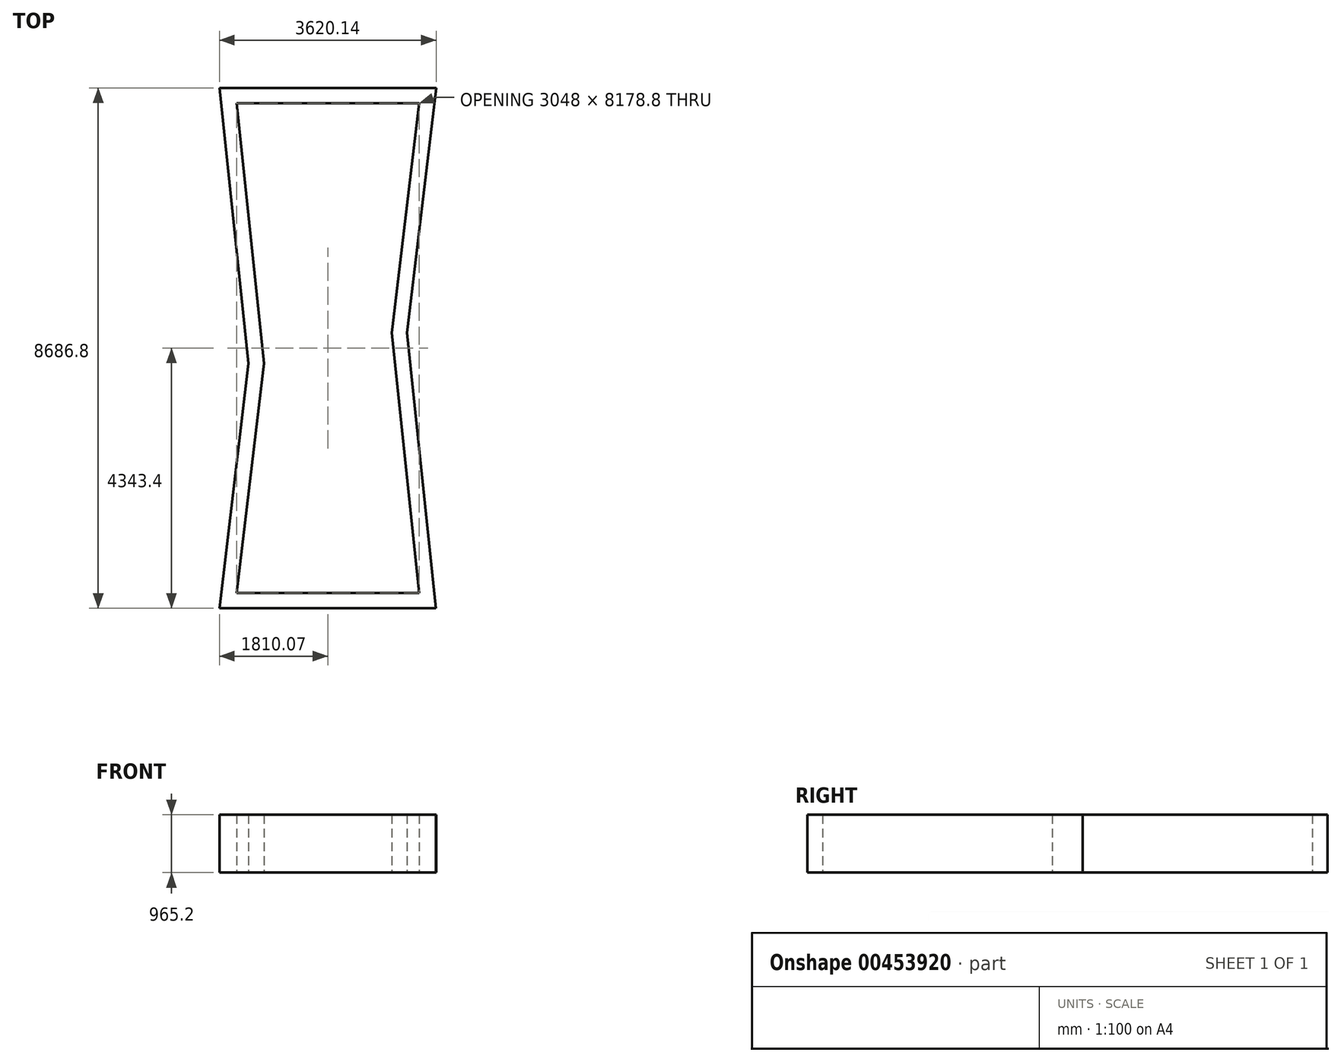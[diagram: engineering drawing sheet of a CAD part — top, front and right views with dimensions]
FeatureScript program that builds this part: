
annotation { "Feature Type Name" : "Feature", "Feature Type Description" : "" }
export const myFeature = defineFeature(function(context is Context, id is Id, definition is map)
    precondition{}
    {
        {
            var Q0;
            Q0=qCreatedBy(makeId("Top.planeOp"),FACE);
            var sketch = newSketch(context, id + "F0", { "sketchPlane" : qUnion([Q0])});
            skLineSegment(sketch, "E0", {"start": v(-1810.07, -4343.4) * mm, "end": v(-1322.38, -252.24) * mm});
            skLineSegment(sketch, "E1", {"start": v(-1322.38, -252.24) * mm, "end": v(-1806.14, 4343.4) * mm});
            skLineSegment(sketch, "E2", {"start": v(-1806.14, 4343.4) * mm, "end": v(1810.07, 4343.4) * mm});
            skLineSegment(sketch, "E3", {"start": v(1810.07, 4343.4) * mm, "end": v(1322.39, 252.24) * mm});
            skLineSegment(sketch, "E4", {"start": v(1322.39, 252.24) * mm, "end": v(1806.14, -4343.4) * mm});
            skLineSegment(sketch, "E5", {"start": v(1806.14, -4343.4) * mm, "end": v(-1810.07, -4343.4) * mm});
            skLineSegment(sketch, "E6", {"start": v(-1524, 4089.4) * mm, "end": v(-1066.8, -254) * mm});
            skLineSegment(sketch, "E7", {"start": v(-1066.8, -254) * mm, "end": v(-1524, -4089.4) * mm});
            skLineSegment(sketch, "E8", {"start": v(-1524, -4089.4) * mm, "end": v(1524, -4089.4) * mm});
            skLineSegment(sketch, "E9", {"start": v(1524, -4089.4) * mm, "end": v(1066.8, 254) * mm});
            skLineSegment(sketch, "E10", {"start": v(1066.8, 254) * mm, "end": v(1524, 4089.4) * mm});
            skLineSegment(sketch, "E11", {"start": v(1524, 4089.4) * mm, "end": v(-1524, 4089.4) * mm});
            skSolve(sketch);
        }
        {
            var Q0;
            Q0=makeQuery(id+"F0.imprint","IMPRINT",FACE,{"disambiguationData":[TD([[makeQuery(id+"F0.imprint","IMPRINT",EDGE,{"derivedFrom":sQuery(id+"F0.wireOp",EDGE,"E0")}),-1.0]])]});
            extrude(context, id + "F1", {"entities" : qUnion([Q0]), "depth" : 965.2 * mm});
        }
    });
